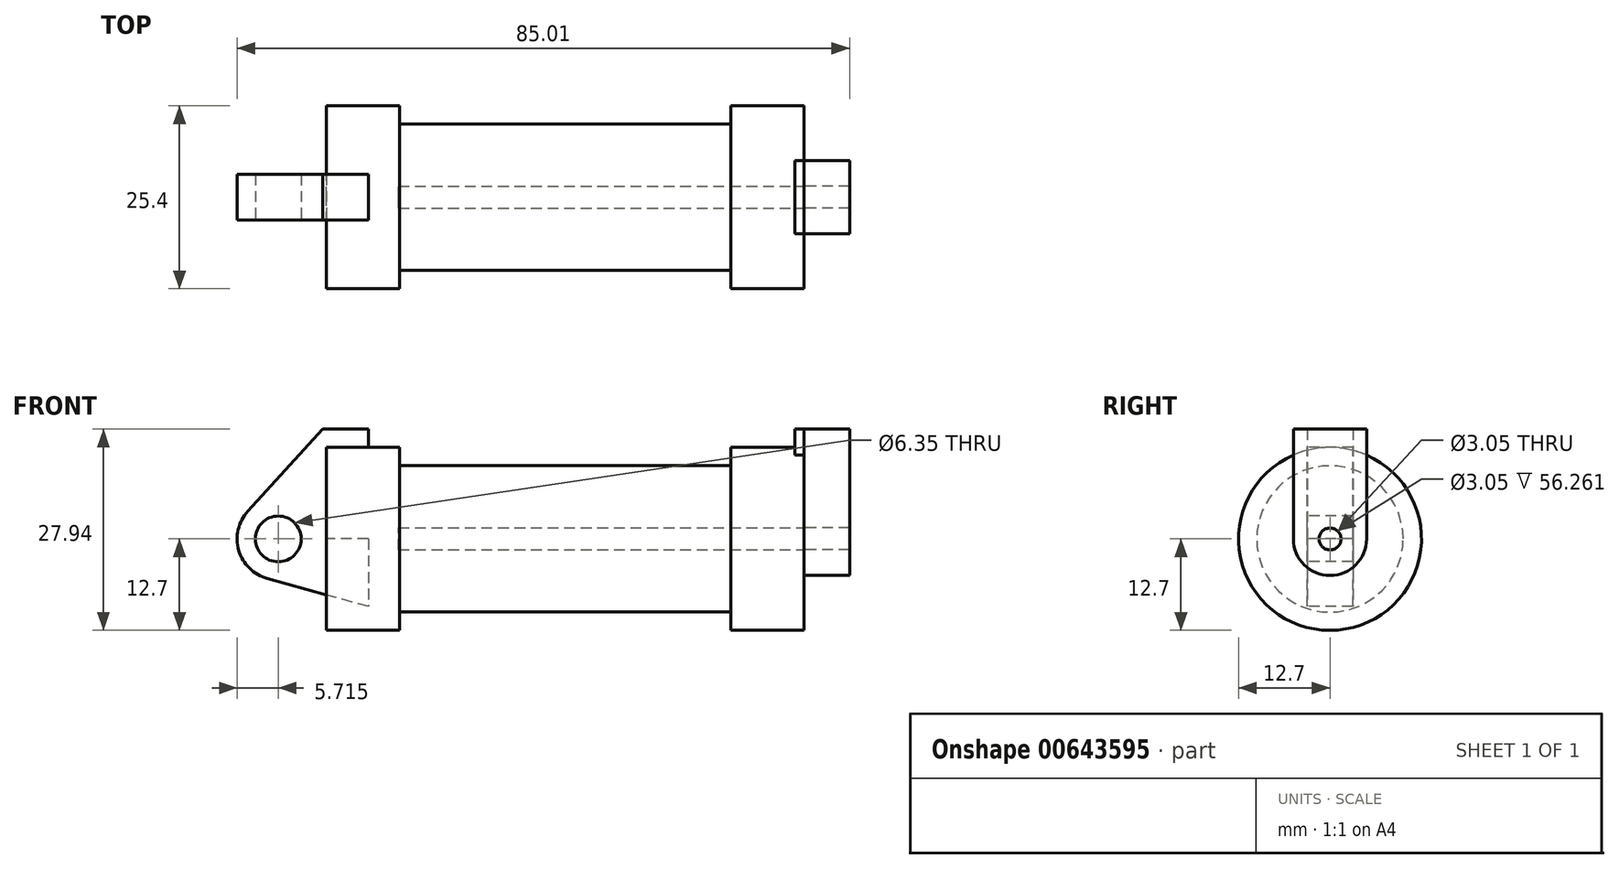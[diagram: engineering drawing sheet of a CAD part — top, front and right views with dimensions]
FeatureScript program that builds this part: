
annotation { "Feature Type Name" : "Feature", "Feature Type Description" : "" }
export const myFeature = defineFeature(function(context is Context, id is Id, definition is map)
    precondition{}
    {
        {
            var Q0;
            Q0=qCreatedBy(makeId("Front.planeOp"),FACE);
            var sketch = newSketch(context, id + "F0", { "sketchPlane" : qUnion([Q0])});
            skLineSegment(sketch, "E0", {"start": v(0, 0) * mm, "end": v(0, 12.7) * mm});
            skLineSegment(sketch, "E1", {"start": v(0, 12.7) * mm, "end": v(10.16, 12.7) * mm});
            skLineSegment(sketch, "E2", {"start": v(10.16, 12.7) * mm, "end": v(10.16, 10.16) * mm});
            skLineSegment(sketch, "E3", {"start": v(10.16, 10.16) * mm, "end": v(56.13, 10.16) * mm});
            skLineSegment(sketch, "E4", {"start": v(56.13, 10.16) * mm, "end": v(56.13, 12.7) * mm});
            skLineSegment(sketch, "E5", {"start": v(56.13, 12.7) * mm, "end": v(66.3, 12.7) * mm});
            skLineSegment(sketch, "E6", {"start": v(66.3, 12.7) * mm, "end": v(66.3, 0) * mm});
            skLineSegment(sketch, "E7", {"start": v(66.3, 0) * mm, "end": v(0, 0) * mm});
            skLineSegment(sketch, "E8", {"start": v(5.84, 15.24) * mm, "end": v(-0.5, 15.24) * mm});
            skLineSegment(sketch, "E9", {"start": v(-0.5, 15.24) * mm, "end": v(-10.88, 3.85) * mm});
            skLineSegment(sketch, "E10", {"start": v(0, 0) * mm, "end": v(-6.65, 0) * mm});
            skCircle(sketch, "E11", {"center": v(-6.65, 0) * mm, "radius": 5.72 * mm});
            skCircle(sketch, "E12", {"center": v(-6.65, 0) * mm, "radius": 3.18 * mm});
            skLineSegment(sketch, "E13", {"start": v(5.84, 15.24) * mm, "end": v(5.84, -9.4) * mm});
            skLineSegment(sketch, "E14", {"start": v(5.84, -9.4) * mm, "end": v(-8.18, -5.5) * mm});
            skSolve(sketch);
        }
        {
            var Q0;
            {var subQ0=sQuery(id+"F0.wireOp",EDGE,"E2");Q0=makeQuery(id+"F0.imprint","IMPRINT",FACE,{"disambiguationData":[TD([[makeQuery(id+"F0.imprint","IMPRINT",EDGE,{"derivedFrom":subQ0}),-1.0]])]});}
            var Q1;
            {var subQ0=sQuery(id+"F0.wireOp",EDGE,"E0");Q1=makeQuery(id+"F0.imprint","IMPRINT",FACE,{"disambiguationData":[TD([[makeQuery(id+"F0.imprint","IMPRINT",EDGE,{"derivedFrom":subQ0}),-1.0]])]});}
            var Q2;
            Q2=sQuery(id+"F0.wireOp",EDGE,"E7");
            revolve(context, id + "F1", {"entities" : qUnion([Q0, Q1]), "axis" : qUnion([Q2]), "revolveType" : RevolveType.FULL});
        }
        {
            var Q0;
            {var subQ1=sQuery(id+"F0.wireOp",EDGE,"E0");Q0=makeQuery(id+"F0.imprint","IMPRINT",FACE,{"disambiguationData":[TD([[makeQuery(id+"F0.imprint","IMPRINT",EDGE,{"derivedFrom":subQ1}),1.0]])]});}
            var Q1;
            {var subQ0=sQuery(id+"F0.wireOp",EDGE,"E14");Q1=makeQuery(id+"F0.imprint","IMPRINT",FACE,{"disambiguationData":[TD([[makeQuery(id+"F0.imprint","IMPRINT",EDGE,{"derivedFrom":subQ0}),-1.0]])]});}
            var Q2;
            {var subQ5=sQuery(id+"F0.wireOp",EDGE,"E12");Q2=makeQuery(id+"F0.imprint","IMPRINT",FACE,{"disambiguationData":[TD([[makeQuery(id+"F0.imprint","IMPRINT",EDGE,{"derivedFrom":subQ5}),-1.0]])]});}
            extrude(context, id + "F2", {"entities" : qUnion([Q0, Q1, Q2]), "endBound" : BoundingType.SYMMETRIC, "oppositeDirection" : true, "depth" : 6.35 * mm, "offsetDistance" : 25.4 * mm});
        }
        {
            var Q0;
            Q0=makeQuery(id+"F1.opRevolve","SWEPT_FACE",FACE,{"disambiguationData":[OSD([sQuery(id+"F0.wireOp",EDGE,"E6")])]});
            var sketch = newSketch(context, id + "F3", { "sketchPlane" : qUnion([Q0])});
            skArc(sketch, "E15", {"start": v(-5.08, 0) * mm, "mid": v(0, -5.08) * mm, "end": v(5.08, 0) * mm});
            skCircle(sketch, "E16", {"center": v(0, 0) * mm, "radius": 1.52 * mm});
            skLineSegment(sketch, "E17", {"start": v(-5.08, 0) * mm, "end": v(-5.08, 15.24) * mm});
            skLineSegment(sketch, "E18", {"start": v(5.08, 0) * mm, "end": v(5.08, 15.24) * mm});
            skLineSegment(sketch, "E19", {"start": v(-5.08, 15.24) * mm, "end": v(5.08, 15.24) * mm});
            skSolve(sketch);
        }
        {
            var Q0;
            {var subQ1=sQuery(id+"F3.wireOp",EDGE,"E15");Q0=makeQuery(id+"F3.imprint","IMPRINT",FACE,{"disambiguationData":[TD([[makeQuery(id+"F3.imprint","IMPRINT",EDGE,{"derivedFrom":subQ1}),1.0]])]});}
            var Q1;
            Q1=makeQuery(id+"F3.imprint","IMPRINT",FACE,{"disambiguationData":[TD([[makeQuery(id+"F3.imprint","IMPRINT",EDGE,{"derivedFrom":sQuery(id+"F3.wireOp",EDGE,"E16")}),1.0]])]});
            var Q2;
            {var subQ0=sQuery(id+"F3.wireOp",EDGE,"E19");Q2=makeQuery(id+"F3.imprint","IMPRINT",FACE,{"disambiguationData":[TD([[makeQuery(id+"F3.imprint","IMPRINT",EDGE,{"derivedFrom":subQ0}),-1.0]])]});}
            extrude(context, id + "F4", {"entities" : qUnion([Q0, Q1, Q2]), "operationType" : NewBodyOperationType.ADD, "oppositeDirection" : true, "depth" : 1.27 * mm, "offsetDistance" : 25.4 * mm});
        }
        {
            var Q0;
            {var subQ0=sQuery(id+"F3.wireOp",EDGE,"E19");Q0=makeQuery(id+"F3.imprint","IMPRINT",FACE,{"disambiguationData":[TD([[makeQuery(id+"F3.imprint","IMPRINT",EDGE,{"derivedFrom":subQ0}),-1.0]])]});}
            var Q1;
            {var subQ1=sQuery(id+"F3.wireOp",EDGE,"E15");Q1=makeQuery(id+"F3.imprint","IMPRINT",FACE,{"disambiguationData":[TD([[makeQuery(id+"F3.imprint","IMPRINT",EDGE,{"derivedFrom":subQ1}),1.0]])]});}
            extrude(context, id + "F5", {"entities" : qUnion([Q0, Q1]), "depth" : 6.35 * mm, "offsetDistance" : 25.4 * mm});
        }
        {
            var Q0;
            Q0=makeQuery(id+"F3.imprint","IMPRINT",FACE,{"disambiguationData":[TD([[makeQuery(id+"F3.imprint","IMPRINT",EDGE,{"derivedFrom":sQuery(id+"F3.wireOp",EDGE,"E16")}),1.0]])]});
            extrude(context, id + "F6", {"entities" : qUnion([Q0]), "operationType" : NewBodyOperationType.REMOVE, "oppositeDirection" : true, "depth" : 56.26 * mm, "offsetDistance" : 25.4 * mm});
        }
    });
